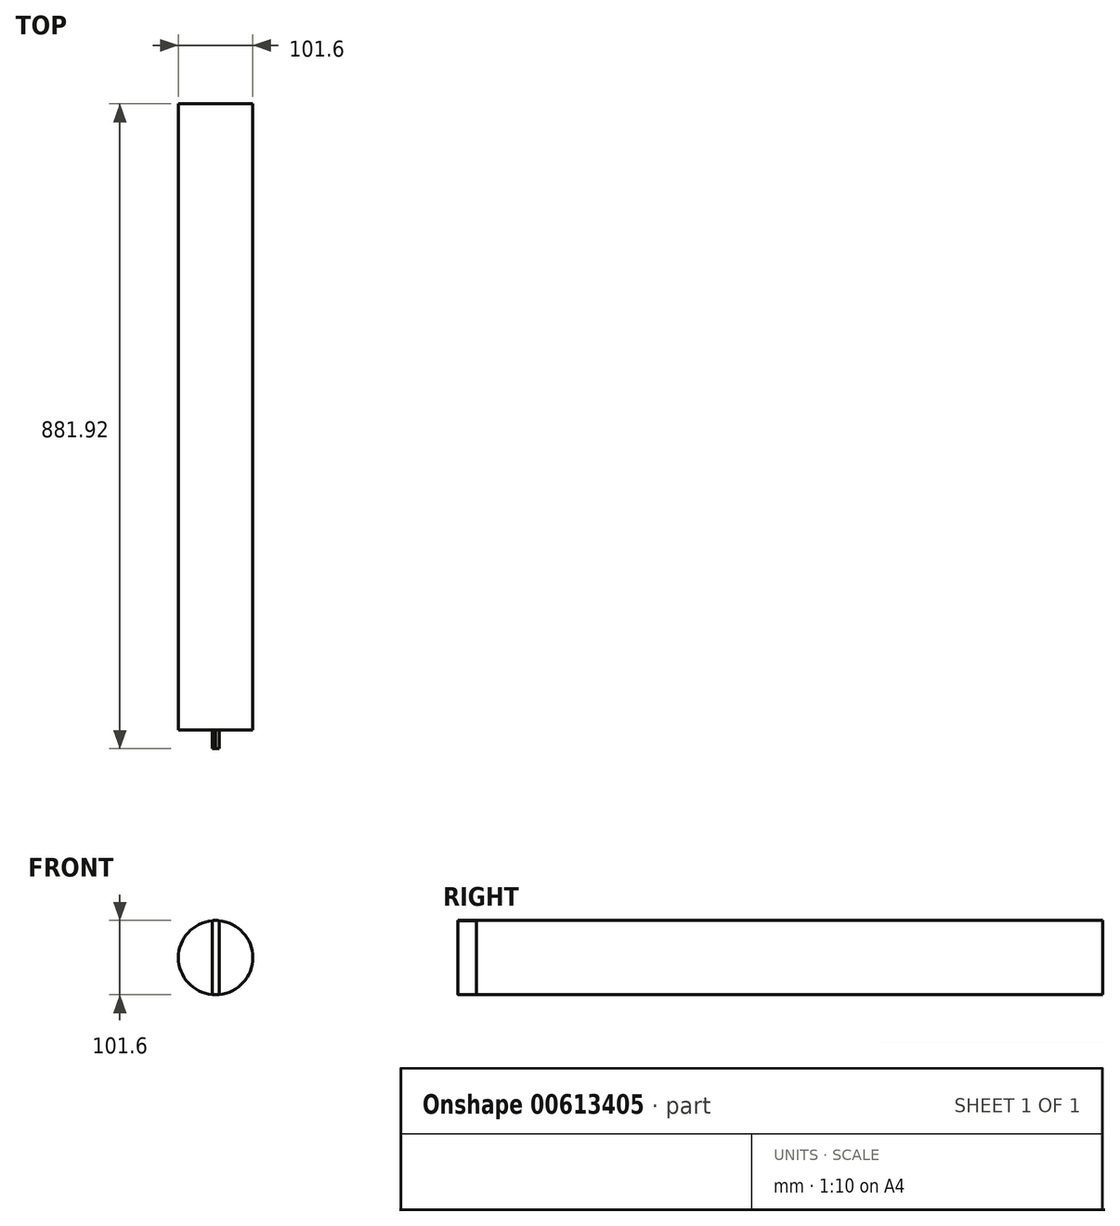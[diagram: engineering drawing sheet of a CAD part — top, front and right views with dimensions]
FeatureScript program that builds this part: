
annotation { "Feature Type Name" : "Feature", "Feature Type Description" : "" }
export const myFeature = defineFeature(function(context is Context, id is Id, definition is map)
    precondition{}
    {
        {
            var Q0;
            Q0=qCreatedBy(makeId("Right.planeOp"),FACE);
            var sketch = newSketch(context, id + "F0", { "sketchPlane" : qUnion([Q0])});
            skLineSegment(sketch, "E0.bottom", {"start": v(428.26, 25.4) * mm, "end": v(-428.26, 25.4) * mm});
            skLineSegment(sketch, "E0.top", {"start": v(428.26, -25.4) * mm, "end": v(-428.26, -25.4) * mm});
            skLineSegment(sketch, "E0.left", {"start": v(428.26, 25.4) * mm, "end": v(428.26, -25.4) * mm});
            skLineSegment(sketch, "E0.right", {"start": v(-428.26, 25.4) * mm, "end": v(-428.26, -25.4) * mm});
            skPoint(sketch, "E0.middle", {"position": v(0, 0) * mm});
            skSolve(sketch);
        }
        {
            var Q0;
            Q0=makeQuery(id+"F0.imprint","IMPRINT",FACE,{"disambiguationData":[TD([[makeQuery(id+"F0.imprint","IMPRINT",EDGE,{"derivedFrom":sQuery(id+"F0.wireOp",EDGE,"E0.bottom")}),1.0]])]});
            var Q1;
            Q1=sQuery(id+"F0.wireOp",EDGE,"E0.bottom");
            var Q2;
            Q2=sQuery(id+"F0.wireOp",EDGE,"E0.top");
            var Q3;
            Q3=sQuery(id+"F0.wireOp",EDGE,"E0.right");
            var Q4;
            Q4=sQuery(id+"F0.wireOp",EDGE,"E0.left");
            var Q5;
            Q5=sQuery(id+"F0.wireOp",EDGE,"E0.bottom");
            revolve(context, id + "F1", {"entities" : qUnion([Q0]), "surfaceEntities" : qUnion([Q1, Q2, Q3, Q4]), "axis" : qUnion([Q5]), "revolveType" : RevolveType.FULL});
        }
        {
            var Q0;
            Q0=makeQuery(id+"F1.opRevolve","SWEPT_FACE",FACE,{"disambiguationData":[OSD([sQuery(id+"F0.wireOp",EDGE,"E0.right")])]});
            var sketch = newSketch(context, id + "F2", { "sketchPlane" : qUnion([Q0])});
            skLineSegment(sketch, "E1", {"start": v(0, -25.4) * mm, "end": v(0, -25.29) * mm});
            skLineSegment(sketch, "E2", {"start": v(-4.8, -25.17) * mm, "end": v(-4.8, 75.97) * mm});
            skLineSegment(sketch, "E3", {"start": v(-4.8, 75.97) * mm, "end": v(0, 76.2) * mm});
            skLineSegment(sketch, "E4.MirrorCS", {"start": v(4.8, -25.17) * mm, "end": v(4.8, 75.97) * mm});
            skLineSegment(sketch, "E5.MirrorCS", {"start": v(4.8, 75.97) * mm, "end": v(0, 76.2) * mm});
            skLineSegment(sketch, "E6.trimOffspring", {"start": v(0, 76.09) * mm, "end": v(0, 76.2) * mm});
            skPoint(sketch, "E7.MirrorCS.end.orphan", {"position": v(4.8, -25.17) * mm});
            skPoint(sketch, "E7.MirrorCS.start.orphan", {"position": v(0, -25.4) * mm});
            skPoint(sketch, "E8.center.orphan", {"position": v(0, 25.4) * mm});
            skSolve(sketch);
        }
        {
            var Q0;
            {var subQ1=sQuery(id+"F2.wireOp",EDGE,"E2");Q0=makeQuery(id+"F2.imprint","IMPRINT",FACE,{"disambiguationData":[TD([[makeQuery(id+"F2.imprint","IMPRINT",EDGE,{"derivedFrom":subQ1}),-1.0]])]});}
            extrude(context, id + "F3", {"entities" : qUnion([Q0]), "operationType" : NewBodyOperationType.ADD, "depth" : 25.4 * mm, "offsetDistance" : 25.4 * mm});
        }
        {
            var Q0;
            {var subQ1=sQuery(id+"F2.wireOp",EDGE,"E2");Q0=makeQuery(id+"F2.imprint","IMPRINT",FACE,{"disambiguationData":[TD([[makeQuery(id+"F2.imprint","IMPRINT",EDGE,{"derivedFrom":subQ1}),-1.0]])]});}
            extrude(context, id + "F4", {"entities" : qUnion([Q0]), "operationType" : NewBodyOperationType.ADD, "oppositeDirection" : true, "depth" : 0.5 * mm, "offsetDistance" : 25.4 * mm});
        }
    });
